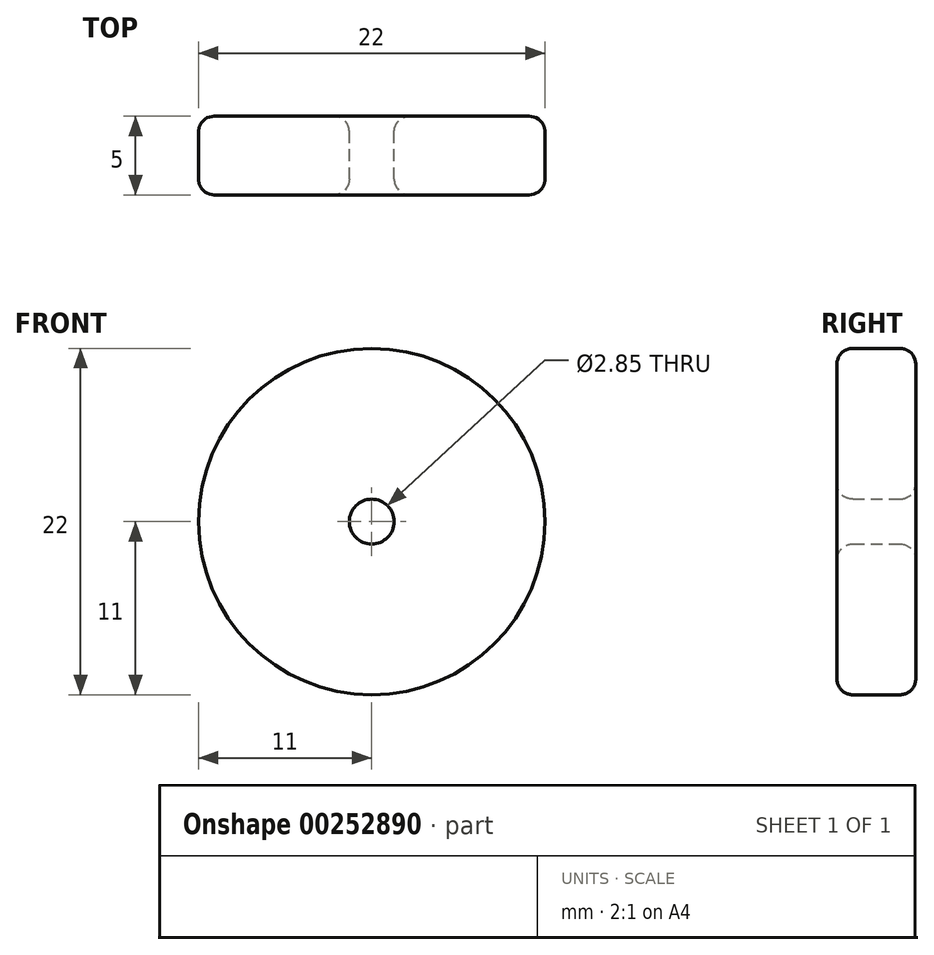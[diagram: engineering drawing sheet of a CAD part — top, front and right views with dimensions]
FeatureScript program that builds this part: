
annotation { "Feature Type Name" : "Feature", "Feature Type Description" : "" }
export const myFeature = defineFeature(function(context is Context, id is Id, definition is map)
    precondition{}
    {
        {
            var Q0;
            Q0=qCreatedBy(makeId("Front.planeOp"),FACE);
            var sketch = newSketch(context, id + "F0", { "sketchPlane" : qUnion([Q0])});
            skCircle(sketch, "E0", {"center": v(0, 0) * mm, "radius": 11 * mm});
            skCircle(sketch, "E1", {"center": v(0, 0) * mm, "radius": 1.43 * mm});
            skSolve(sketch);
        }
        {
            var Q0;
            Q0=makeQuery(id+"F0.imprint","IMPRINT",FACE,{"disambiguationData":[TD([[makeQuery(id+"F0.imprint","IMPRINT",EDGE,{"derivedFrom":sQuery(id+"F0.wireOp",EDGE,"E0")}),1.0]])]});
            extrude(context, id + "F1", {"entities" : qUnion([Q0]), "depth" : 5 * mm});
        }
        {
            var Q0;
            Q0=makeQuery(id+"F1.opExtrude","CAP_EDGE",EDGE,{"disambiguationData":[OSD([sQuery(id+"F0.wireOp",EDGE,"E1")])],"isStart":false});
            fillet(context, id + "F2", {"entities" : qUnion([Q0]), "radius" : 1 * mm, "tangentPropagation" : true, "allowEdgeOverflow" : false});
        }
        {
            var Q0;
            Q0=makeQuery(id+"F1.opExtrude","CAP_EDGE",EDGE,{"disambiguationData":[OSD([sQuery(id+"F0.wireOp",EDGE,"E1")])],"isStart":true});
            fillet(context, id + "F3", {"entities" : qUnion([Q0]), "radius" : 1 * mm, "tangentPropagation" : true, "allowEdgeOverflow" : false});
        }
        {
            var Q0;
            Q0=makeQuery(id+"F1.opExtrude","CAP_EDGE",EDGE,{"disambiguationData":[OSD([sQuery(id+"F0.wireOp",EDGE,"E0")])],"isStart":false});
            fillet(context, id + "F4", {"entities" : qUnion([Q0]), "radius" : 1 * mm, "tangentPropagation" : true, "allowEdgeOverflow" : false});
        }
        {
            var Q0;
            Q0=makeQuery(id+"F1.opExtrude","CAP_EDGE",EDGE,{"disambiguationData":[OSD([sQuery(id+"F0.wireOp",EDGE,"E0")])],"isStart":true});
            fillet(context, id + "F5", {"entities" : qUnion([Q0]), "radius" : 1 * mm, "tangentPropagation" : true, "allowEdgeOverflow" : false});
        }
    });
